# Revit family: Genie_Site_ArticulatingBoom_(Z-30-20N)a
name_source: partatom
category: Site
revit_build: Autodesk Revit 2018 (Build: 20190510_1515(x64)
units: mm (PartAtom-declared; Revit-internal decimal feet)

## family parameters
Always vertical = Yes
Cut with Voids When Loaded = No
OmniClass Number = 23.50.85.17
OmniClass Title = Telescoping Platforms
Part Type = Normal
Round Connector Dimension = Use Diameter
Shared = No
Work Plane-Based = No

## types (1)
- Z-30-20N
    Assembly Code = E1030900
    AssetType = Fixed
    BIMObjectName = Genie_Site_ArticulatingBoom_(Z-30-20N)
    ClassificationName = Uniclass2015
    ClassificationValue = Pr_65_80_47_95
    Color = Grey & Blue
    Cost = 0 $
    Description = The Genie® Z®-30/20 N RJ articulating boom lift offers quiet, emission-free operation in the most sensitive work environments, and includes a rotating jib for 180°of horizontal rotation. Similar to the Z®-30/20 N, when the machine must be driven significant distances, the Genie bi-energy system combines the benefits of a 48V DC machine with the versatility of a diesel-powered generator.
    DocumentationLiterature = http://genielift.com.au
    DocumentationTechnical = http://genielift.com.au
    DurationUnit = Years
    ExpectedLife = 0
    Features = Works in tight spaces with zero tailswing and front arm swing in stowed and raised positions. Compact chassis for narrow aisle access. The RJ model features a rotating jib that adds an industry-leading 180° (2 x 90°) of horizontal rotation. 35% gradeability drive performance and 3.3 mph travel speed.
    Finish = Painted Steel
    IfcExportAs = IfcTransportElement
    IfcExportType = IfcTransportElementType
    Keynote = X
    Manufacturer = Genie
    ManufacturerName = Genie
    Material = Painted Steel
    Model = Genie - Articulating Boom
    ModelNumber = Z-30-20N
    ModelReference = Genie - Articulating Boom
    NBSDescription = Vertical lifting platforms
    NBSObjectName = Genie - Vertical lifting platforms
    NBSReference = 90-80-65/350
    NominalDepth = 1190 mm  [stored 3.9042 ft]
    NominalHeight = 2000 mm  [stored 6.56168 ft]
    NominalLength = 5310 mm  [stored 17.4213 ft]
    ProductionYear = 2018
    ReplacementCost = 0
    Size = 1.19m x 2m x 5.31m
    Type Comments = Z-30-20N
    TypeName = Genie - Articulating Boom
    URL = http://www.genielift.co.uk
    WarrantyDurationLabor = 0
    WarrantyDurationParts = 0
    WarrantyDurationUnit = Years
    WarrantyGuarantorLabor = http://www.genielift.co.uk
    WarrantyGuarantorParts = http://www.genielift.co.uk
    _BSBibleVersion = 15
    _BimSpecGuid = 0
    _CurrentRevision = 1
    _DistributedBy = www.bimstore.co.uk

note: [stored X ft] marks values corroborated as IEEE doubles in the binary element streams (Revit-internal decimal feet)

## geometry (parser evidence)
native form markers: Sweep x46
no freeform markers — native parametric forms only
